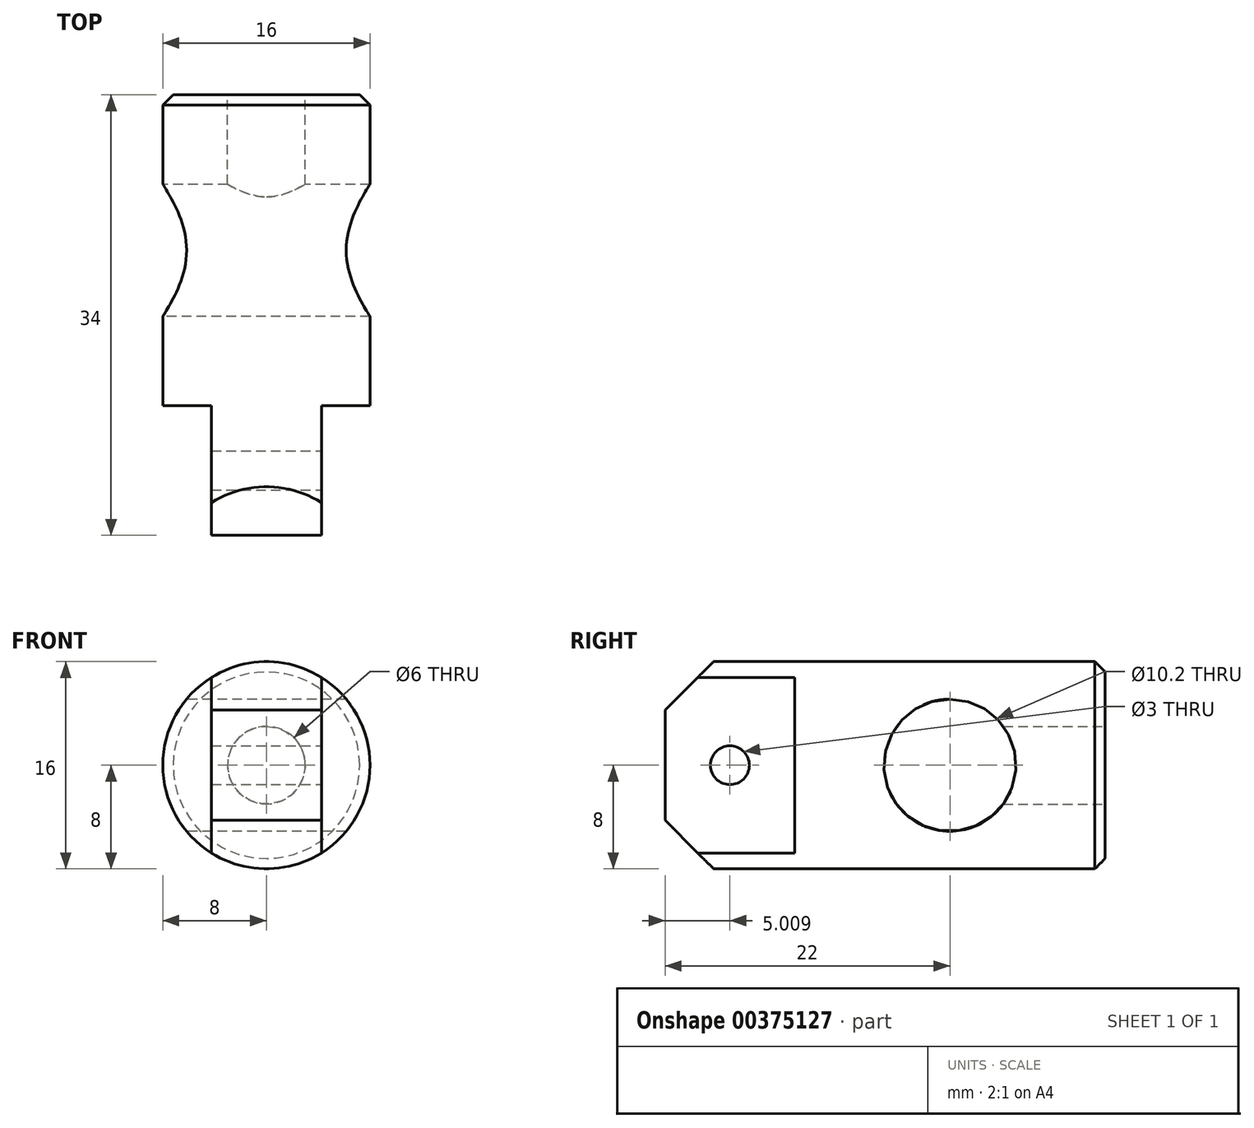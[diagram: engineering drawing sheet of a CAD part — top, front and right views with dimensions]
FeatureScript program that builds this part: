
annotation { "Feature Type Name" : "Feature", "Feature Type Description" : "" }
export const myFeature = defineFeature(function(context is Context, id is Id, definition is map)
    precondition{}
    {
        {
            var Q0;
            Q0=qCreatedBy(makeId("Front.planeOp"),FACE);
            var sketch = newSketch(context, id + "F0", { "sketchPlane" : qUnion([Q0])});
            skCircle(sketch, "E0", {"center": v(0, 0) * mm, "radius": 8 * mm});
            skSolve(sketch);
        }
        {
            var Q0;
            Q0=makeQuery(id+"F0.imprint","IMPRINT",FACE,{"disambiguationData":[TD([[makeQuery(id+"F0.imprint","IMPRINT",EDGE,{"derivedFrom":sQuery(id+"F0.wireOp",EDGE,"E0")}),1.0]])]});
            extrude(context, id + "F1", {"entities" : qUnion([Q0]), "depth" : 34 * mm});
        }
        {
            var Q0;
            Q0=makeQuery(id+"F1.opExtrude","CAP_FACE",FACE,{"disambiguationData":[OSD([sQuery(id+"F0.wireOp",EDGE,"E0")])],"isStart":false});
            var sketch = newSketch(context, id + "F2", { "sketchPlane" : qUnion([Q0])});
            skLineSegment(sketch, "E1", {"start": v(0, 0) * mm, "end": v(4.25, 0) * mm});
            skLineSegment(sketch, "E2", {"start": v(0, 0) * mm, "end": v(-4.25, 0) * mm});
            skLineSegment(sketch, "E3", {"start": v(-4.25, 0) * mm, "end": v(-4.25, -6.78) * mm});
            skLineSegment(sketch, "E4", {"start": v(-4.25, -6.78) * mm, "end": v(-4.25, 6.78) * mm});
            skLineSegment(sketch, "E5", {"start": v(4.25, 0) * mm, "end": v(4.25, 6.78) * mm});
            skLineSegment(sketch, "E6", {"start": v(4.25, 0) * mm, "end": v(4.25, -6.78) * mm});
            skSolve(sketch);
        }
        {
            var Q0;
            {var subQ0=sQuery(id+"F2.wireOp",EDGE,"E4");var subQ1=makeQuery(id+"F2.imprint","INTERSECT",VERTEX,{"derivedFrom":[sQuery(id+"F2.wireOp",EDGE,"E2"),subQ0]});Q0=makeQuery(id+"F2.imprint","IMPRINT",FACE,{"disambiguationData":[TD([[makeQuery(id+"F2.imprint","IMPRINT",EDGE,{"disambiguationData":[TD([[subQ1,1.0]])],"derivedFrom":subQ0}),1.0]])]});}
            var Q1;
            {var subQ0=sQuery(id+"F2.wireOp",EDGE,"E5");Q1=makeQuery(id+"F2.imprint","IMPRINT",FACE,{"disambiguationData":[TD([[makeQuery(id+"F2.imprint","IMPRINT",EDGE,{"derivedFrom":subQ0}),-1.0]])]});}
            extrude(context, id + "F3", {"entities" : qUnion([Q0, Q1]), "operationType" : NewBodyOperationType.REMOVE, "oppositeDirection" : true, "depth" : 10 * mm});
        }
        {
            var Q0;
            Q0=makeQuery(id+"F3.boolean.opBoolean","COPY",FACE,{"derivedFrom":makeQuery(id+"F3.opExtrude","SWEPT_FACE",FACE,{"disambiguationData":[OSD([sQuery(id+"F2.wireOp",EDGE,"E4")])]})});
            var sketch = newSketch(context, id + "F4", { "sketchPlane" : qUnion([Q0])});
            skLineSegment(sketch, "E7", {"start": v(34, 0) * mm, "end": v(34, 4.25) * mm});
            skLineSegment(sketch, "E8", {"start": v(34, 4.25) * mm, "end": v(34, -4.25) * mm});
            skLineSegment(sketch, "E9", {"start": v(34, -4.25) * mm, "end": v(27.49, -10.76) * mm});
            skLineSegment(sketch, "E10", {"start": v(34, 4.25) * mm, "end": v(29, 9.25) * mm});
            skPoint(sketch, "E10.endSnap0", {"position": v(29, 6.78) * mm});
            skLineSegment(sketch, "E11", {"start": v(29, 9.25) * mm, "end": v(38.66, 9.25) * mm});
            skLineSegment(sketch, "E12", {"start": v(38.66, 9.25) * mm, "end": v(38.66, 4.54) * mm});
            skLineSegment(sketch, "E13", {"start": v(38.66, 4.54) * mm, "end": v(34, 4.25) * mm});
            skLineSegment(sketch, "E14", {"start": v(27.7, -10.56) * mm, "end": v(43.54, -10.56) * mm});
            skLineSegment(sketch, "E15", {"start": v(43.54, -10.56) * mm, "end": v(42.48, -4.28) * mm});
            skLineSegment(sketch, "E16", {"start": v(42.48, -4.28) * mm, "end": v(34, -4.25) * mm});
            skSolve(sketch);
        }
        {
            var Q0;
            {var subQ0=sQuery(id+"F4.wireOp",EDGE,"E10");var subQ1=sQuery(id+"F2.wireOp",EDGE,"E4");var subQ4=sQuery(id+"F0.wireOp",EDGE,"E0");var subQ5=makeQuery(id+"F3.boolean.opBoolean","COPY",EDGE,{"derivedFrom":makeQuery(id+"F3.opExtrude","SWEPT_EDGE",EDGE,{"disambiguationData":[OSD([subQ4,subQ1]),TDD([makeQuery(id+"F2.imprint","INTERSECT",VERTEX,{"disambiguationData":[OD(1.0)],"derivedFrom":[makeQuery(id+"F1.opExtrude","CAP_EDGE",EDGE,{"disambiguationData":[OSD([subQ4])],"isStart":false}),subQ1]})])]})});var subQ6=makeQuery(id+"F4.imprint","INTERSECT",VERTEX,{"derivedFrom":[subQ5,subQ0]});Q0=makeQuery(id+"F4.imprint","IMPRINT",FACE,{"disambiguationData":[TD([[makeQuery(id+"F4.imprint","IMPRINT",EDGE,{"disambiguationData":[TD([[subQ6,1.0]])],"derivedFrom":subQ0}),-1.0]])]});}
            var Q1;
            {var subQ1=sQuery(id+"F4.wireOp",EDGE,"E11");Q1=makeQuery(id+"F4.imprint","IMPRINT",FACE,{"disambiguationData":[TD([[makeQuery(id+"F4.imprint","IMPRINT",EDGE,{"derivedFrom":subQ1}),-1.0]])]});}
            extrude(context, id + "F5", {"entities" : qUnion([Q0, Q1]), "operationType" : NewBodyOperationType.REMOVE, "oppositeDirection" : true, "depth" : 25 * mm});
        }
        {
            var Q0;
            {var subQ0=sQuery(id+"F4.wireOp",EDGE,"E9");var subQ1=sQuery(id+"F2.wireOp",EDGE,"E4");var subQ4=sQuery(id+"F0.wireOp",EDGE,"E0");var subQ5=makeQuery(id+"F3.boolean.opBoolean","COPY",EDGE,{"derivedFrom":makeQuery(id+"F3.opExtrude","SWEPT_EDGE",EDGE,{"disambiguationData":[OSD([subQ4,subQ1]),TDD([makeQuery(id+"F2.imprint","INTERSECT",VERTEX,{"disambiguationData":[OD(0.0)],"derivedFrom":[makeQuery(id+"F1.opExtrude","CAP_EDGE",EDGE,{"disambiguationData":[OSD([subQ4])],"isStart":false}),subQ1]})])]})});var subQ6=makeQuery(id+"F4.imprint","INTERSECT",VERTEX,{"derivedFrom":[subQ5,subQ0]});Q0=makeQuery(id+"F4.imprint","IMPRINT",FACE,{"disambiguationData":[TD([[makeQuery(id+"F4.imprint","IMPRINT",EDGE,{"disambiguationData":[TD([[subQ6,1.0]])],"derivedFrom":subQ0}),1.0]])]});}
            var Q1;
            {var subQ1=sQuery(id+"F4.wireOp",EDGE,"E14");Q1=makeQuery(id+"F4.imprint","IMPRINT",FACE,{"disambiguationData":[TD([[makeQuery(id+"F4.imprint","IMPRINT",EDGE,{"derivedFrom":subQ1}),1.0]])]});}
            extrude(context, id + "F6", {"entities" : qUnion([Q0, Q1]), "operationType" : NewBodyOperationType.REMOVE, "oppositeDirection" : true, "depth" : 25 * mm});
        }
        {
            var Q0;
            Q0=qCreatedBy(makeId("Right.planeOp"),FACE);
            var sketch = newSketch(context, id + "F7", { "sketchPlane" : qUnion([Q0])});
            skLineSegment(sketch, "E17", {"start": v(-34, 0) * mm, "end": v(-29, 0) * mm});
            skSolve(sketch);
        }
        {
            var Q0;
            Q0=sQuery(id+"F7.wireOp",VERTEX,"E17.end");
            var Q1;
            Q1=makeQuery(id+"F1.opExtrude","SWEPT_BODY",BODY,{"disambiguationData":[OSD([sQuery(id+"F0.wireOp",EDGE,"E0")])]});
            hole(context, id + "F8", {"style" : HoleStyle.SIMPLE, "endStyle" : HoleEndStyle.THROUGH, "holeDiameter" : 3 * mm, "isTappedThrough" : true, "tappedDepth" : 12 * mm, "tapClearance" : 3, "startFromSketch" : true, "locations" : qUnion([Q0]), "scope" : qUnion([Q1])});
        }
        {
            var Q0;
            Q0=sQuery(id+"F7.wireOp",VERTEX,"E17.end");
            var Q1;
            Q1=makeQuery(id+"F1.opExtrude","SWEPT_BODY",BODY,{"disambiguationData":[OSD([sQuery(id+"F0.wireOp",EDGE,"E0")])]});
            hole(context, id + "F9", {"style" : HoleStyle.SIMPLE, "endStyle" : HoleEndStyle.THROUGH, "oppositeDirection" : true, "holeDiameter" : 3 * mm, "isTappedThrough" : true, "tappedDepth" : 12 * mm, "tapClearance" : 3, "startFromSketch" : true, "locations" : qUnion([Q0]), "scope" : qUnion([Q1])});
        }
        {
            var Q0;
            Q0=qCreatedBy(makeId("Right.planeOp"),FACE);
            var sketch = newSketch(context, id + "F10", { "sketchPlane" : qUnion([Q0])});
            skLineSegment(sketch, "E18", {"start": v(0, 0) * mm, "end": v(-12, 0) * mm});
            skSolve(sketch);
        }
        {
            var Q0;
            Q0=sQuery(id+"F10.wireOp",VERTEX,"E18.end");
            var Q1;
            Q1=makeQuery(id+"F1.opExtrude","SWEPT_BODY",BODY,{"disambiguationData":[OSD([sQuery(id+"F0.wireOp",EDGE,"E0")])]});
            hole(context, id + "F11", {"style" : HoleStyle.SIMPLE, "endStyle" : HoleEndStyle.THROUGH, "oppositeDirection" : true, "holeDiameter" : 10.2 * mm, "isTappedThrough" : true, "tappedDepth" : 12 * mm, "tapClearance" : 3, "startFromSketch" : true, "locations" : qUnion([Q0]), "scope" : qUnion([Q1])});
        }
        {
            var Q0;
            Q0=sQuery(id+"F10.wireOp",VERTEX,"E18.end");
            var Q1;
            Q1=makeQuery(id+"F1.opExtrude","SWEPT_BODY",BODY,{"disambiguationData":[OSD([sQuery(id+"F0.wireOp",EDGE,"E0")])]});
            hole(context, id + "F12", {"style" : HoleStyle.SIMPLE, "endStyle" : HoleEndStyle.THROUGH, "holeDiameter" : 10.2 * mm, "isTappedThrough" : true, "tappedDepth" : 12 * mm, "tapClearance" : 3, "startFromSketch" : true, "locations" : qUnion([Q0]), "scope" : qUnion([Q1])});
        }
        {
            var Q0;
            Q0=makeQuery(id+"F1.opExtrude","CAP_EDGE",EDGE,{"disambiguationData":[OSD([sQuery(id+"F0.wireOp",EDGE,"E0")])],"isStart":true});
            chamfer(context, id + "F13", {"entities" : qUnion([Q0]), "width" : 0.8 * mm, "tangentPropagation" : true});
        }
        {
            var Q0;
            Q0=makeQuery(id+"F0.imprint","IMPRINT",FACE,{"disambiguationData":[TD([[makeQuery(id+"F0.imprint","IMPRINT",EDGE,{"derivedFrom":sQuery(id+"F0.wireOp",EDGE,"E0")}),1.0]])]});
            var sketch = newSketch(context, id + "F14", { "sketchPlane" : qUnion([Q0])});
            skCircle(sketch, "E19", {"center": v(0, 0) * mm, "radius": 3 * mm});
            skSolve(sketch);
        }
        {
            var Q0;
            Q0=sQuery(id+"F14.wireOp",VERTEX,"E19.center");
            var Q1;
            Q1=makeQuery(id+"F1.opExtrude","SWEPT_BODY",BODY,{"disambiguationData":[OSD([sQuery(id+"F0.wireOp",EDGE,"E0")])]});
            hole(context, id + "F15", {"style" : HoleStyle.SIMPLE, "endStyle" : HoleEndStyle.BLIND, "oppositeDirection" : true, "holeDiameter" : 6 * mm, "holeDepth" : 15 * mm, "isTappedThrough" : true, "tappedDepth" : 12 * mm, "tapClearance" : 3, "startFromSketch" : true, "locations" : qUnion([Q0]), "scope" : qUnion([Q1])});
        }
    });
